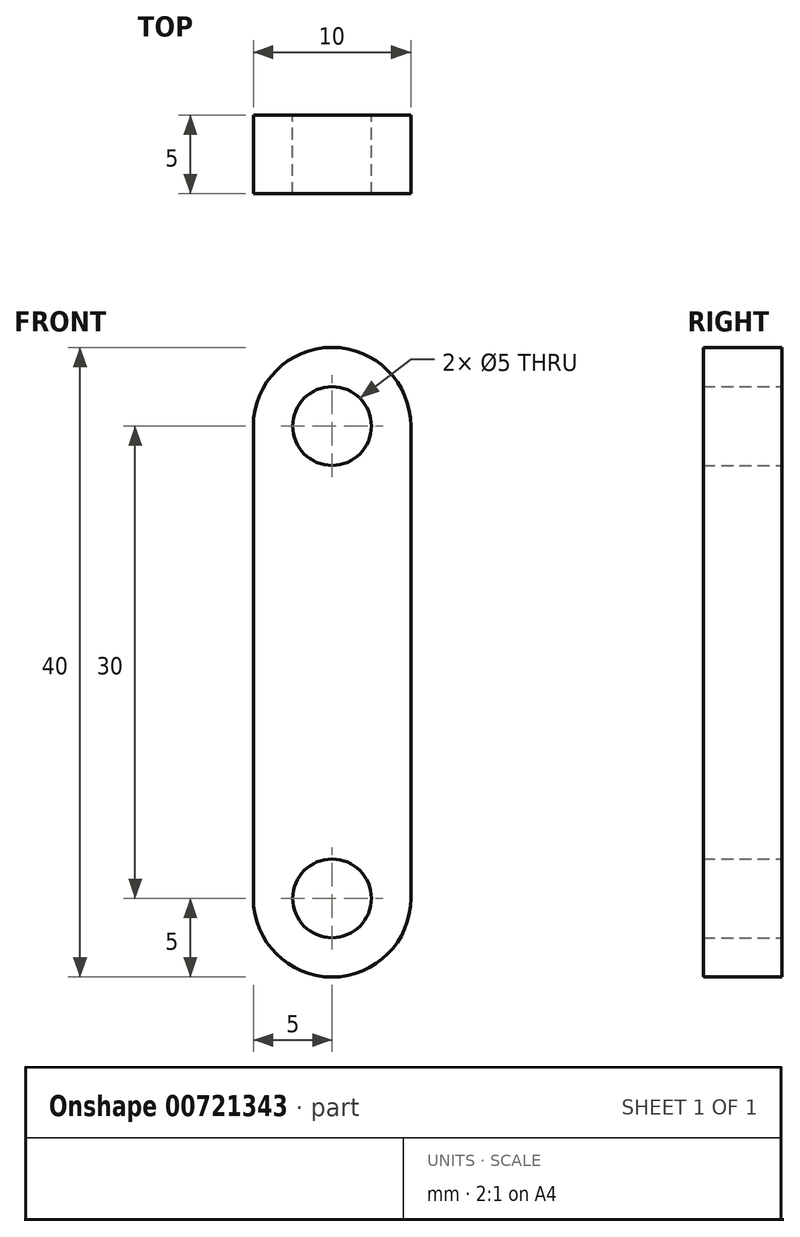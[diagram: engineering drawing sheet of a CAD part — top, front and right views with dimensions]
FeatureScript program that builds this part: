
annotation { "Feature Type Name" : "Feature", "Feature Type Description" : "" }
export const myFeature = defineFeature(function(context is Context, id is Id, definition is map)
    precondition{}
    {
        {
            var Q0;
            Q0=qCreatedBy(makeId("Front.planeOp"),FACE);
            var sketch = newSketch(context, id + "F0", { "sketchPlane" : qUnion([Q0])});
            skLineSegment(sketch, "E0.left", {"start": v(5, 15) * mm, "end": v(5, -15) * mm});
            skLineSegment(sketch, "E0.right", {"start": v(-5, 15) * mm, "end": v(-5, -15) * mm});
            skPoint(sketch, "E0.middle", {"position": v(0, 0) * mm});
            skArc(sketch, "E1", {"start": v(5, 15) * mm, "mid": v(0, 20) * mm, "end": v(-5, 15) * mm});
            skArc(sketch, "E2", {"start": v(-5, -15) * mm, "mid": v(0, -20) * mm, "end": v(5, -15) * mm});
            skCircle(sketch, "E3", {"center": v(0, -15) * mm, "radius": 2.5 * mm});
            skCircle(sketch, "E4", {"center": v(0, 15) * mm, "radius": 2.5 * mm});
            skSolve(sketch);
        }
        {
            var Q0;
            Q0 = qSketchRegion(id + "F0", true);
            extrude(context, id + "F1", {"entities" : qUnion([Q0]), "depth" : 5 * mm, "offsetDistance" : 25.4 * mm});
        }
    });
